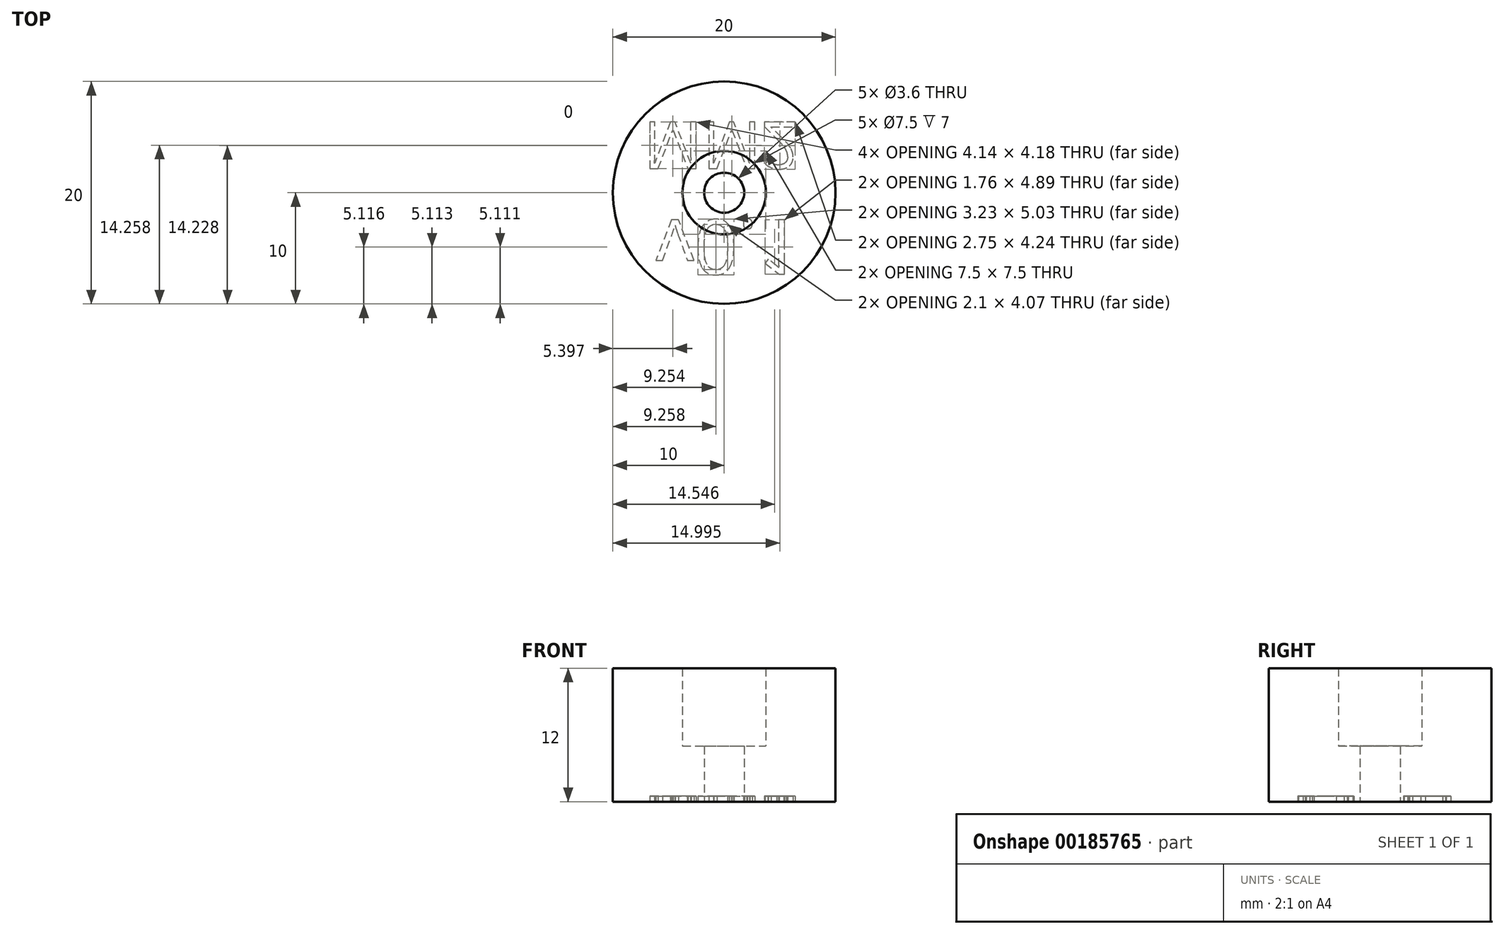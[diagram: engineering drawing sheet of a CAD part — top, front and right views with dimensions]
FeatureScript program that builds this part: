
annotation { "Feature Type Name" : "Feature", "Feature Type Description" : "" }
export const myFeature = defineFeature(function(context is Context, id is Id, definition is map)
    precondition{}
    {
        {
            var Q0;
            Q0=qCreatedBy(makeId("Top.planeOp"),FACE);
            var sketch = newSketch(context, id + "F0", { "sketchPlane" : qUnion([Q0])});
            skCircle(sketch, "E0", {"center": v(0, 0) * mm, "radius": 10 * mm});
            skSolve(sketch);
        }
        {
            var Q0;
            Q0 = qSketchRegion(id + "F0", true);
            extrude(context, id + "F1", {"entities" : qUnion([Q0]), "depth" : 12 * mm});
        }
        {
            var Q0;
            Q0=makeQuery(id+"F1.opExtrude","CAP_FACE",FACE,{"disambiguationData":[OSD([sQuery(id+"F0.wireOp",EDGE,"E0")])],"isStart":true});
            var sketch = newSketch(context, id + "F2", { "sketchPlane" : qUnion([Q0])});
            skCircle(sketch, "E1", {"center": v(0, 0) * mm, "radius": 1.8 * mm});
            skSolve(sketch);
        }
        {
            var Q0;
            Q0 = qSketchRegion(id + "F2", true);
            extrude(context, id + "F3", {"entities" : qUnion([Q0]), "operationType" : NewBodyOperationType.REMOVE, "oppositeDirection" : true, "depth" : 5 * mm});
        }
        {
            var Q0;
            Q0=makeQuery(id+"F3.boolean.opBoolean","COPY",FACE,{"derivedFrom":makeQuery(id+"F3.opExtrude","CAP_FACE",FACE,{"disambiguationData":[OSD([sQuery(id+"F2.wireOp",EDGE,"E1")])],"isStart":false})});
            var sketch = newSketch(context, id + "F4", { "sketchPlane" : qUnion([Q0])});
            skCircle(sketch, "E2", {"center": v(0, 0) * mm, "radius": 3.75 * mm});
            skSolve(sketch);
        }
        {
            var Q0;
            Q0 = qSketchRegion(id + "F4", true);
            extrude(context, id + "F5", {"entities" : qUnion([Q0]), "operationType" : NewBodyOperationType.REMOVE, "oppositeDirection" : true, "depth" : 25 * mm});
        }
        {
            var Q0;
            Q0=makeQuery(id+"F1.opExtrude","CAP_FACE",FACE,{"disambiguationData":[OSD([sQuery(id+"F0.wireOp",EDGE,"E0")])],"isStart":true});
            var sketch = newSketch(context, id + "F6", { "sketchPlane" : qUnion([Q0])});
            skText(sketch, "E3", { "text": "v0.1 ", "fontName": "OpenSans-Regular.ttf"});
            const initialGuessF6  = {"E3": [-0.00613, 0.00244, 1, 0, 0.00493]};
            skSetInitialGuess(sketch, initialGuessF6);
            skSolve(sketch);
        }
        {
            var Q0;
            Q0 = qSketchRegion(id + "F6", true);
            extrude(context, id + "F7", {"entities" : qUnion([Q0]), "operationType" : NewBodyOperationType.REMOVE, "oppositeDirection" : true, "depth" : .5 * mm});
        }
        {
            var Q0;
            {var subQ0=sQuery(id+"F0.wireOp",EDGE,"E0");Q0=makeQuery(id+"F7.boolean.opBoolean","SPLIT",FACE,{"disambiguationData":[TD([makeQuery(id+"F1.opExtrude","SWEPT_FACE",FACE,{"disambiguationData":[OSD([subQ0])]})])],"derivedFrom":makeQuery(id+"F1.opExtrude","CAP_FACE",FACE,{"disambiguationData":[OSD([subQ0])],"isStart":true})});}
            var sketch = newSketch(context, id + "F8", { "sketchPlane" : qUnion([Q0])});
            skText(sketch, "E4", { "text": "MM2", "fontName": "OpenSans-Regular.ttf"});
            const initialGuessF8  = {"E4": [-0.00725, -0.00635, 1, 0, 0.00422]};
            skSetInitialGuess(sketch, initialGuessF8);
            skSolve(sketch);
        }
        {
            var Q0;
            Q0 = qSketchRegion(id + "F8", true);
            extrude(context, id + "F9", {"entities" : qUnion([Q0]), "operationType" : NewBodyOperationType.REMOVE, "oppositeDirection" : true, "depth" : .5 * mm});
        }
    });
